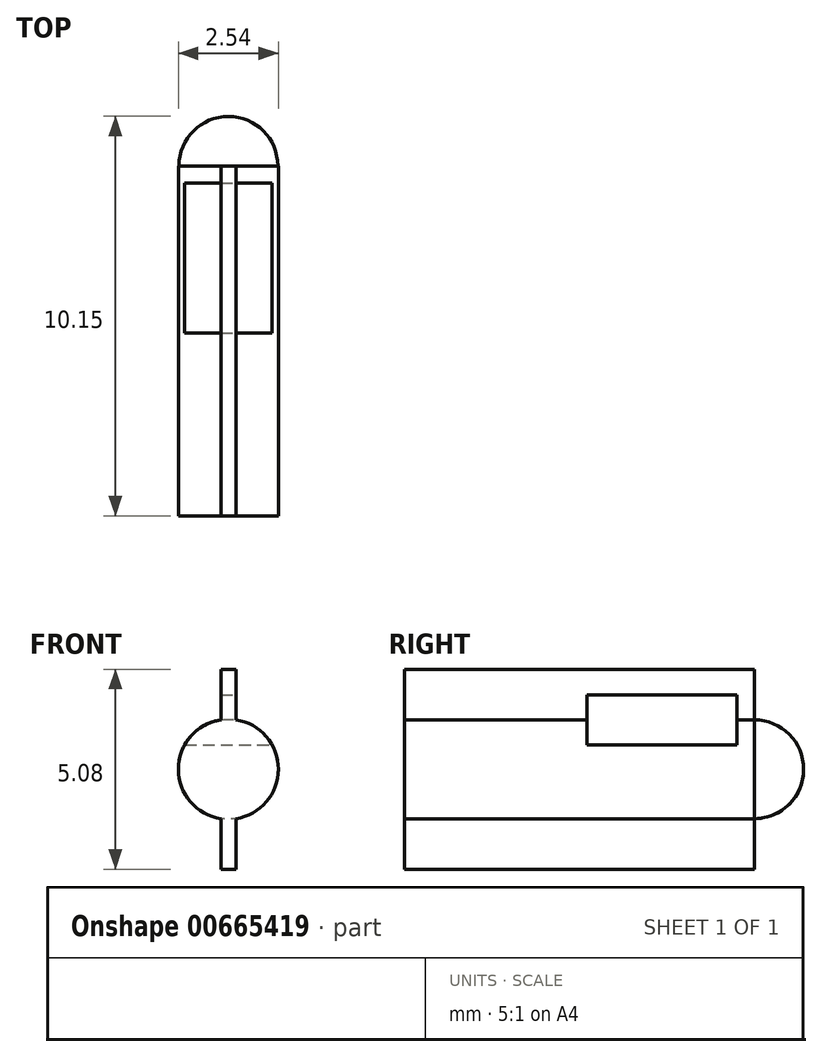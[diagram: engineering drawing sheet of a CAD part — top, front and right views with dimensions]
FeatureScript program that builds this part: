
annotation { "Feature Type Name" : "Feature", "Feature Type Description" : "" }
export const myFeature = defineFeature(function(context is Context, id is Id, definition is map)
    precondition{}
    {
        {
            var Q0;
            Q0=qCreatedBy(makeId("Front.planeOp"),FACE);
            var sketch = newSketch(context, id + "F0", { "sketchPlane" : qUnion([Q0])});
            skArc(sketch, "E0", {"start": v(0.2, -1.26) * mm, "mid": v(1.27, 0) * mm, "end": v(0.2, 1.26) * mm});
            skLineSegment(sketch, "E1.top", {"start": v(0.2, 2.54) * mm, "end": v(-0.2, 2.54) * mm});
            skLineSegment(sketch, "E1.left", {"start": v(0.2, 1.26) * mm, "end": v(0.2, 2.54) * mm});
            skLineSegment(sketch, "E1.right", {"start": v(-0.2, 1.26) * mm, "end": v(-0.2, 2.54) * mm});
            skLineSegment(sketch, "E2.top", {"start": v(0.2, -2.54) * mm, "end": v(-0.2, -2.54) * mm});
            skLineSegment(sketch, "E2.left", {"start": v(0.2, -1.26) * mm, "end": v(0.2, -2.54) * mm});
            skLineSegment(sketch, "E2.right", {"start": v(-0.2, -1.26) * mm, "end": v(-0.2, -2.54) * mm});
            skArc(sketch, "E3.trimOffspring", {"start": v(-0.2, 1.26) * mm, "mid": v(-1.27, 0) * mm, "end": v(-0.2, -1.26) * mm});
            skSolve(sketch);
        }
        {
            var Q0;
            Q0=makeQuery(id+"F0.imprint","IMPRINT",FACE,{"disambiguationData":[TD([[makeQuery(id+"F0.imprint","IMPRINT",EDGE,{"derivedFrom":sQuery(id+"F0.wireOp",EDGE,"E0")}),1.0]])]});
            extrude(context, id + "F1", {"entities" : qUnion([Q0]), "depth" : 8.9 * mm, "offsetDistance" : 25.4 * mm});
        }
        {
            var Q0;
            Q0=qCreatedBy(makeId("Right.planeOp"),FACE);
            var sketch = newSketch(context, id + "F2", { "sketchPlane" : qUnion([Q0])});
            skArc(sketch, "E4", {"start": v(0, -1.26) * mm, "mid": v(0.89, -0.89) * mm, "end": v(1.26, 0) * mm});
            skLineSegment(sketch, "E5", {"start": v(0, 0) * mm, "end": v(0, -1.26) * mm});
            skLineSegment(sketch, "E6", {"start": v(0, -1.26) * mm, "end": v(0, 0) * mm});
            skLineSegment(sketch, "E7", {"start": v(1.26, 0) * mm, "end": v(0, 0) * mm});
            skSolve(sketch);
        }
        {
            var Q0;
            Q0=makeQuery(id+"F2.imprint","IMPRINT",FACE,{"disambiguationData":[TD([[makeQuery(id+"F2.imprint","IMPRINT",EDGE,{"derivedFrom":sQuery(id+"F2.wireOp",EDGE,"E4")}),1.0]])]});
            var Q1;
            Q1=sQuery(id+"F2.wireOp",EDGE,"E7");
            revolve(context, id + "F3", {"operationType" : NewBodyOperationType.ADD, "surfaceOperationType" : NewSurfaceOperationType.NEW, "entities" : qUnion([Q0]), "axis" : qUnion([Q1]), "revolveType" : RevolveType.FULL});
        }
        {
            var Q0;
            Q0=makeQuery(id+"F1.opExtrude","SWEPT_FACE",FACE,{"disambiguationData":[OSD([sQuery(id+"F0.wireOp",EDGE,"E1.left")])]});
            var sketch = newSketch(context, id + "F4", { "sketchPlane" : qUnion([Q0])});
            skLineSegment(sketch, "E8.bottom", {"start": v(-0.44, 0.62) * mm, "end": v(-4.25, 0.62) * mm});
            skLineSegment(sketch, "E8.top", {"start": v(-0.44, 1.9) * mm, "end": v(-4.25, 1.9) * mm});
            skLineSegment(sketch, "E8.left", {"start": v(-0.44, 0.62) * mm, "end": v(-0.44, 1.9) * mm});
            skLineSegment(sketch, "E8.right", {"start": v(-4.25, 0.62) * mm, "end": v(-4.25, 1.9) * mm});
            skPoint(sketch, "E8.middle", {"position": v(-2.34, 1.26) * mm});
            skSolve(sketch);
        }
        {
            var Q0;
            Q0 = qSketchRegion(id + "F4", true);
            extrude(context, id + "F5", {"entities" : qUnion([Q0]), "operationType" : NewBodyOperationType.REMOVE, "oppositeDirection" : true, "depth" : 25.4 * mm, "offsetDistance" : 25.4 * mm, "symmetric" : true});
        }
    });
